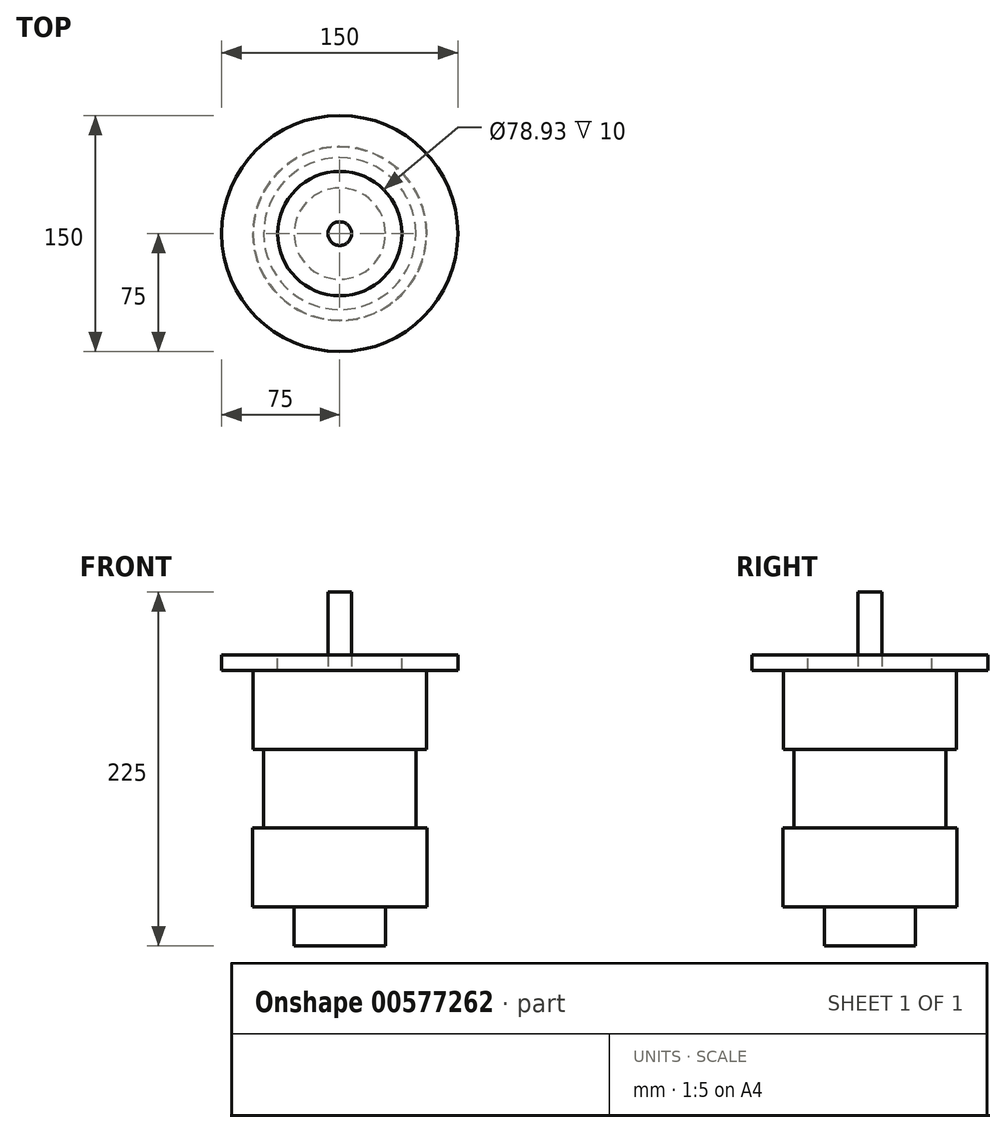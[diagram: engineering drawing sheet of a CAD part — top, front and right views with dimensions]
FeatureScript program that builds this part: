
annotation { "Feature Type Name" : "Feature", "Feature Type Description" : "" }
export const myFeature = defineFeature(function(context is Context, id is Id, definition is map)
    precondition{}
    {
        {
            var Q0;
            Q0=qCreatedBy(makeId("Top.planeOp"),FACE);
            var sketch = newSketch(context, id + "F0", { "sketchPlane" : qUnion([Q0])});
            skCircle(sketch, "E0", {"center": v(0, 0) * mm, "radius": 55 * mm});
            skSolve(sketch);
        }
        {
            var Q0;
            Q0=qSketchRegion(id+"F0",true);
            extrude(context, id + "F1", {"entities" : qUnion([Q0]), "depth" : 50 * mm, "offsetDistance" : 25 * mm});
        }
        {
            var Q0;
            Q0=makeQuery(id+"F1.opExtrude","CAP_FACE",FACE,{"disambiguationData":[OSD([sQuery(id+"F0.wireOp",EDGE,"E0")])],"isStart":false});
            var sketch = newSketch(context, id + "F2", { "sketchPlane" : qUnion([Q0])});
            skCircle(sketch, "E1", {"center": v(0, 0) * mm, "radius": 75 * mm});
            skSolve(sketch);
        }
        {
            var Q0;
            Q0=qSketchRegion(id+"F2",true);
            extrude(context, id + "F3", {"entities" : qUnion([Q0]), "operationType" : NewBodyOperationType.ADD, "depth" : 10 * mm, "offsetDistance" : 25 * mm});
        }
        {
            var Q0;
            Q0=makeQuery(id+"F1.opExtrude","CAP_FACE",FACE,{"disambiguationData":[OSD([sQuery(id+"F0.wireOp",EDGE,"E0")])],"isStart":true});
            var sketch = newSketch(context, id + "F4", { "sketchPlane" : qUnion([Q0])});
            skCircle(sketch, "E2", {"center": v(0, 0) * mm, "radius": 48.29 * mm});
            skSolve(sketch);
        }
        {
            var Q0;
            Q0=qSketchRegion(id+"F4",true);
            extrude(context, id + "F5", {"entities" : qUnion([Q0]), "operationType" : NewBodyOperationType.ADD, "depth" : 50 * mm, "offsetDistance" : 25 * mm});
        }
        {
            var Q0;
            Q0=makeQuery(id+"F5.opExtrude","CAP_FACE",FACE,{"disambiguationData":[OSD([sQuery(id+"F4.wireOp",EDGE,"E2")])],"isStart":false});
            var sketch = newSketch(context, id + "F6", { "sketchPlane" : qUnion([Q0])});
            skCircle(sketch, "E3", {"center": v(0, 0) * mm, "radius": 55.3 * mm});
            skSolve(sketch);
        }
        {
            var Q0;
            Q0=qSketchRegion(id+"F6",true);
            extrude(context, id + "F7", {"entities" : qUnion([Q0]), "operationType" : NewBodyOperationType.ADD, "depth" : 50 * mm, "offsetDistance" : 25 * mm});
        }
        {
            var Q0;
            Q0=makeQuery(id+"F3.opExtrude","CAP_FACE",FACE,{"disambiguationData":[OSD([sQuery(id+"F2.wireOp",EDGE,"E1")])],"isStart":false});
            var sketch = newSketch(context, id + "F8", { "sketchPlane" : qUnion([Q0])});
            skCircle(sketch, "E4", {"center": v(0, 0) * mm, "radius": 39.47 * mm});
            skSolve(sketch);
        }
        {
            var Q0;
            Q0=qSketchRegion(id+"F8",true);
            extrude(context, id + "F9", {"entities" : qUnion([Q0]), "operationType" : NewBodyOperationType.REMOVE, "oppositeDirection" : true, "depth" : 10 * mm, "offsetDistance" : 25 * mm});
        }
        {
            var Q0;
            Q0=makeQuery(id+"F9.boolean.opBoolean","COPY",FACE,{"derivedFrom":makeQuery(id+"F9.opExtrude","CAP_FACE",FACE,{"disambiguationData":[OSD([sQuery(id+"F8.wireOp",EDGE,"E4")])],"isStart":false})});
            var sketch = newSketch(context, id + "F10", { "sketchPlane" : qUnion([Q0])});
            skCircle(sketch, "E5", {"center": v(0, 0) * mm, "radius": 7.5 * mm});
            skSolve(sketch);
        }
        {
            var Q0;
            Q0=qSketchRegion(id+"F10",true);
            extrude(context, id + "F11", {"entities" : qUnion([Q0]), "operationType" : NewBodyOperationType.ADD, "depth" : 50 * mm, "offsetDistance" : 25 * mm});
        }
        {
            var Q0;
            Q0=makeQuery(id+"F7.opExtrude","CAP_FACE",FACE,{"disambiguationData":[OSD([sQuery(id+"F6.wireOp",EDGE,"E3")])],"isStart":false});
            var sketch = newSketch(context, id + "F12", { "sketchPlane" : qUnion([Q0])});
            skCircle(sketch, "E6", {"center": v(0, 0) * mm, "radius": 29 * mm});
            skSolve(sketch);
        }
        {
            var Q0;
            Q0=qSketchRegion(id+"F12",true);
            extrude(context, id + "F13", {"entities" : qUnion([Q0]), "operationType" : NewBodyOperationType.ADD, "depth" : 25 * mm, "offsetDistance" : 25 * mm});
        }
    });
